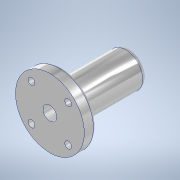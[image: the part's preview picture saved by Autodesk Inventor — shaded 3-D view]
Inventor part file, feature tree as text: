
AUTODESK INVENTOR PART (.ipt)
format: ipt  version: 2020.3 (Build 243373000, 373)  size: 162,816 bytes
history: native  units: mm
features: fillet x3, sketch x3, extrude x2, other x1, hole x1
ambient origin geometry x8: Origin, YZ Plane, XZ Plane, XY Plane, X Axis, Y Axis, Z Axis, Center Point
bodies: Body1 (feature_tree)
feature tree (10):
  other  "ソリッド1"
  extrude  "押し出し1"  Depth=15.0mm
  extrude  "押し出し2"  Depth=6.0mm
  hole  "穴1"  [1 undecoded]
  fillet  "フィレット1"  Radius=6.0mm
  fillet  "フィレット2"  Radius=30.0mm
  fillet  "フィレット3"  Radius=5.0mm
  sketch  "スケッチ1"
  sketch  "スケッチ2"
  sketch  "スケッチ3"
note: 1 required parameter value undecoded (feature->parameter linkage not recoverable at this tier; creation-order binding heuristic only, values carry confidence <= 0.55)
